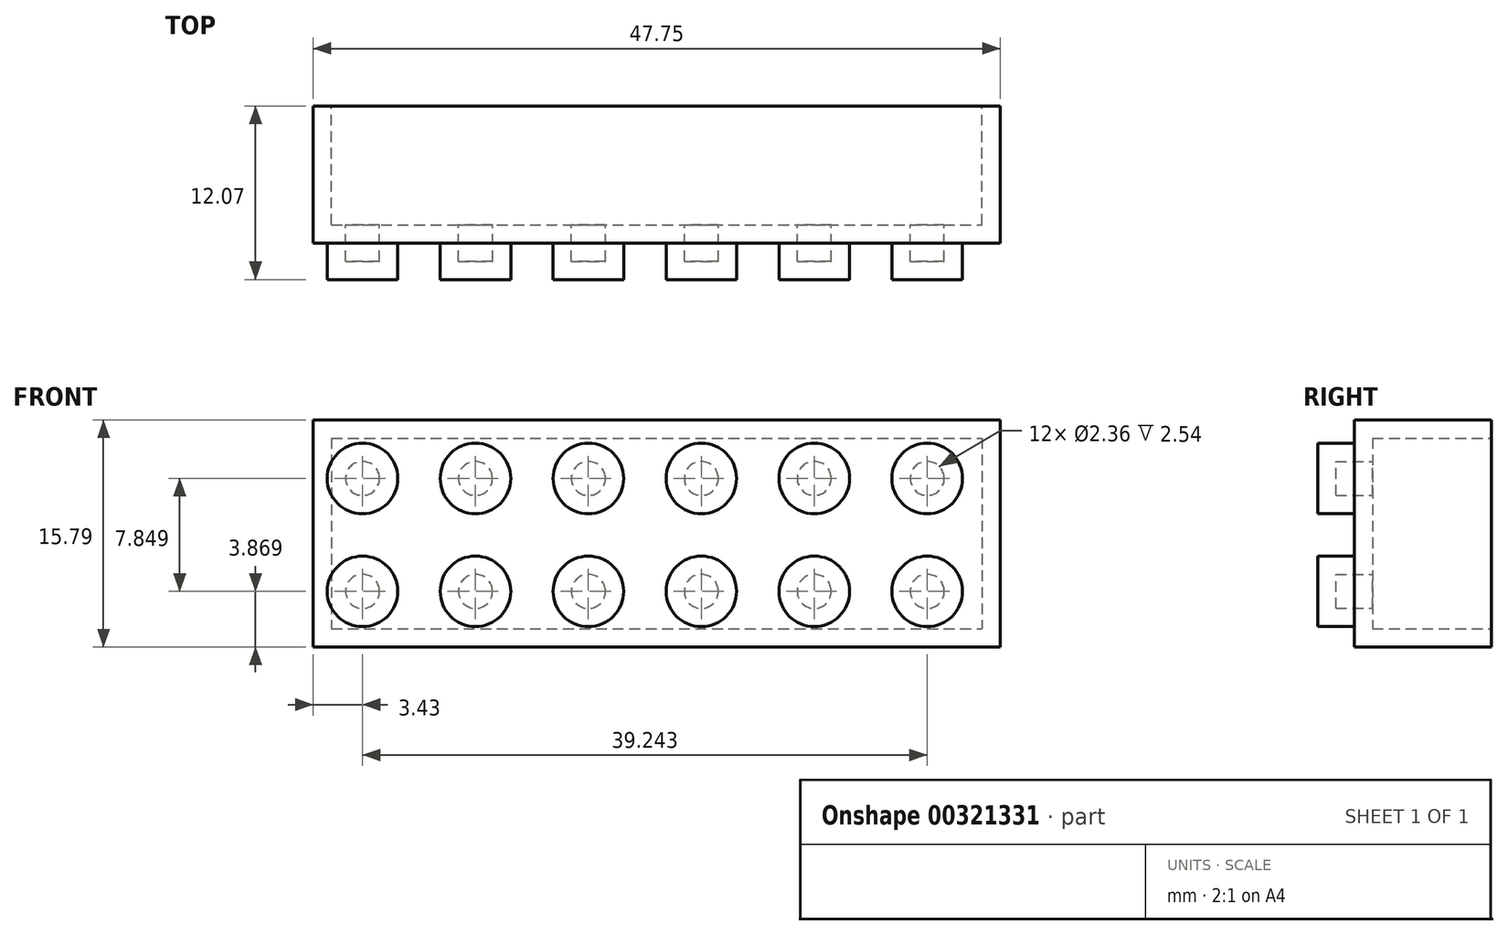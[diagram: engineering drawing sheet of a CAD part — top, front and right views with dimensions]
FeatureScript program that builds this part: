
annotation { "Feature Type Name" : "Feature", "Feature Type Description" : "" }
export const myFeature = defineFeature(function(context is Context, id is Id, definition is map)
    precondition{}
    {
        {
            var Q0;
            Q0=qCreatedBy(makeId("Front.planeOp"),FACE);
            var sketch = newSketch(context, id + "F0", { "sketchPlane" : qUnion([Q0])});
            skLineSegment(sketch, "E0.bottom", {"start": v(-34.22, 31.61) * mm, "end": v(13.53, 31.61) * mm});
            skLineSegment(sketch, "E0.top", {"start": v(-34.22, 15.82) * mm, "end": v(13.53, 15.82) * mm});
            skLineSegment(sketch, "E0.left", {"start": v(-34.22, 31.61) * mm, "end": v(-34.22, 15.82) * mm});
            skLineSegment(sketch, "E0.right", {"start": v(13.53, 31.61) * mm, "end": v(13.53, 15.82) * mm});
            skSolve(sketch);
        }
        {
            var Q0;
            Q0=makeQuery(id+"F0.imprint","IMPRINT",FACE,{"disambiguationData":[TD([[makeQuery(id+"F0.imprint","IMPRINT",EDGE,{"derivedFrom":sQuery(id+"F0.wireOp",EDGE,"E0.bottom")}),-1.0]])]});
            extrude(context, id + "F1", {"entities" : qUnion([Q0]), "depth" : 9.53 * mm});
        }
        {
            var Q0;
            Q0=makeQuery(id+"F1.opExtrude","CAP_FACE",FACE,{"disambiguationData":[OSD([sQuery(id+"F0.wireOp",EDGE,"E0.bottom"),sQuery(id+"F0.wireOp",EDGE,"E0.top"),sQuery(id+"F0.wireOp",EDGE,"E0.left"),sQuery(id+"F0.wireOp",EDGE,"E0.right")])],"isStart":false});
            var sketch = newSketch(context, id + "F2", { "sketchPlane" : qUnion([Q0])});
            skCircle(sketch, "E1", {"center": v(8.45, 27.54) * mm, "radius": 2.45 * mm});
            skCircle(sketch, "E2.0.1.0", {"center": v(8.45, 19.69) * mm, "radius": 2.45 * mm});
            skCircle(sketch, "E2.1.0.0", {"center": v(0.6, 27.54) * mm, "radius": 2.45 * mm});
            skCircle(sketch, "E2.1.1.0", {"center": v(0.6, 19.69) * mm, "radius": 2.45 * mm});
            skCircle(sketch, "E2.2.0.0", {"center": v(-7.24, 27.54) * mm, "radius": 2.45 * mm});
            skCircle(sketch, "E2.2.1.0", {"center": v(-7.24, 19.69) * mm, "radius": 2.45 * mm});
            skCircle(sketch, "E2.3.0.0", {"center": v(-15.1, 27.54) * mm, "radius": 2.45 * mm});
            skCircle(sketch, "E2.3.1.0", {"center": v(-15.1, 19.69) * mm, "radius": 2.45 * mm});
            skCircle(sketch, "E2.4.0.0", {"center": v(-22.94, 27.54) * mm, "radius": 2.45 * mm});
            skCircle(sketch, "E2.4.1.0", {"center": v(-22.94, 19.69) * mm, "radius": 2.45 * mm});
            skCircle(sketch, "E2.5.0.0", {"center": v(-30.8, 27.54) * mm, "radius": 2.45 * mm});
            skCircle(sketch, "E2.5.1.0", {"center": v(-30.8, 19.69) * mm, "radius": 2.45 * mm});
            skLineSegment(sketch, "E2.direction1", {"start": v(8.45, 27.54) * mm, "end": v(0.6, 27.54) * mm, "construction": true});
            skLineSegment(sketch, "E2.direction2", {"start": v(8.45, 27.54) * mm, "end": v(8.45, 19.69) * mm, "construction": true});
            skSolve(sketch);
        }
        {
            var Q0;
            Q0 = qSketchRegion(id + "F2", true);
            extrude(context, id + "F3", {"entities" : qUnion([Q0]), "operationType" : NewBodyOperationType.ADD, "depth" : 2.54 * mm});
        }
        {
            var Q0;
            Q0=makeQuery(id+"F1.opExtrude","CAP_FACE",FACE,{"disambiguationData":[OSD([sQuery(id+"F0.wireOp",EDGE,"E0.bottom"),sQuery(id+"F0.wireOp",EDGE,"E0.top"),sQuery(id+"F0.wireOp",EDGE,"E0.left"),sQuery(id+"F0.wireOp",EDGE,"E0.right")])],"isStart":true});
            shell(context, id + "F4", {"entities" : qUnion([Q0]), "thickness" : 1.27 * mm});
        }
    });
